# Revit family: FAM6_63_UN_Spot_ETK
name_source: partatom
category: Lighting Fixtures
revit_build: Autodesk Revit 2017 (Build: 20190508_0315(x64)
units: mm (PartAtom-declared; Revit-internal decimal feet)

## family parameters
Always vertical = Yes
Cut with Voids When Loaded = Yes
Light Source = No
OmniClass Number = 23.80.70.11.14.11
OmniClass Title = Downlights
Part Type = Normal
Room Calculation Point = Yes
Round Connector Dimension = Use Diameter
Shared = No
Work Plane-Based = No

## types (9) — shared parameters
Apparent Load = 8 VA
Assembly Code = 63.0
Bundle = 42°
IfcExportAs = IfcLightFixtureType
IfcExportType = USERDEFINED
Lamp = LED
Manufacturer = ETK licht B.V.
Material = RAL 9003
Model = FAM.6
Type Comments = IP65
URL = https://www.etk.nl
Voltage = 230 V
Wattage Comments = 8W

## per-type parameters (varying)
| type | Light Source |
| FAM.6101.xx - 8W / 640lm / 2700K | FAM.6 - Lightsource : FAM.6101.xx - 8W / 640lm / 2700K |
| FAM.6201.xx - 8W / 680lm / 3000K | FAM.6 - Lightsource : FAM.6201.xx - 8W / 680lm / 3000K |
| FAM.6301.xx - 8W / 730lm / 4000K | FAM.6 - Lightsource : FAM.6301.xx - 8W / 730lm / 4000K |
| FAM.6102.xx - 8W / 640lm / 2700K | FAM.6 - Lightsource : FAM.6102.xx - 8W / 640lm / 2700K |
| FAM.6103.xx - 8W / 640lm / 2700K | FAM.6 - Lightsource : FAM.6103.xx - 8W / 640lm / 2700K |
| FAM.6202.xx - 8W / 680lm / 3000K | FAM.6 - Lightsource : FAM.6202.xx - 8W / 680lm / 3000K |
| FAM.6203.xx - 8W / 680lm / 3000K | FAM.6 - Lightsource : FAM.6203.xx - 8W / 680lm / 3000K |
| FAM.6302.xx - 8W / 730lm / 4000K | FAM.6 - Lightsource : FAM.6202.xx - 8W / 680lm / 3000K |
| FAM.6303.xx - 8W / 730lm / 4000K | FAM.6 - Lightsource : FAM.6303.xx - 8W / 730lm / 4000K |

## geometry (parser evidence)
native form markers: Sweep x4
no freeform markers — native parametric forms only
